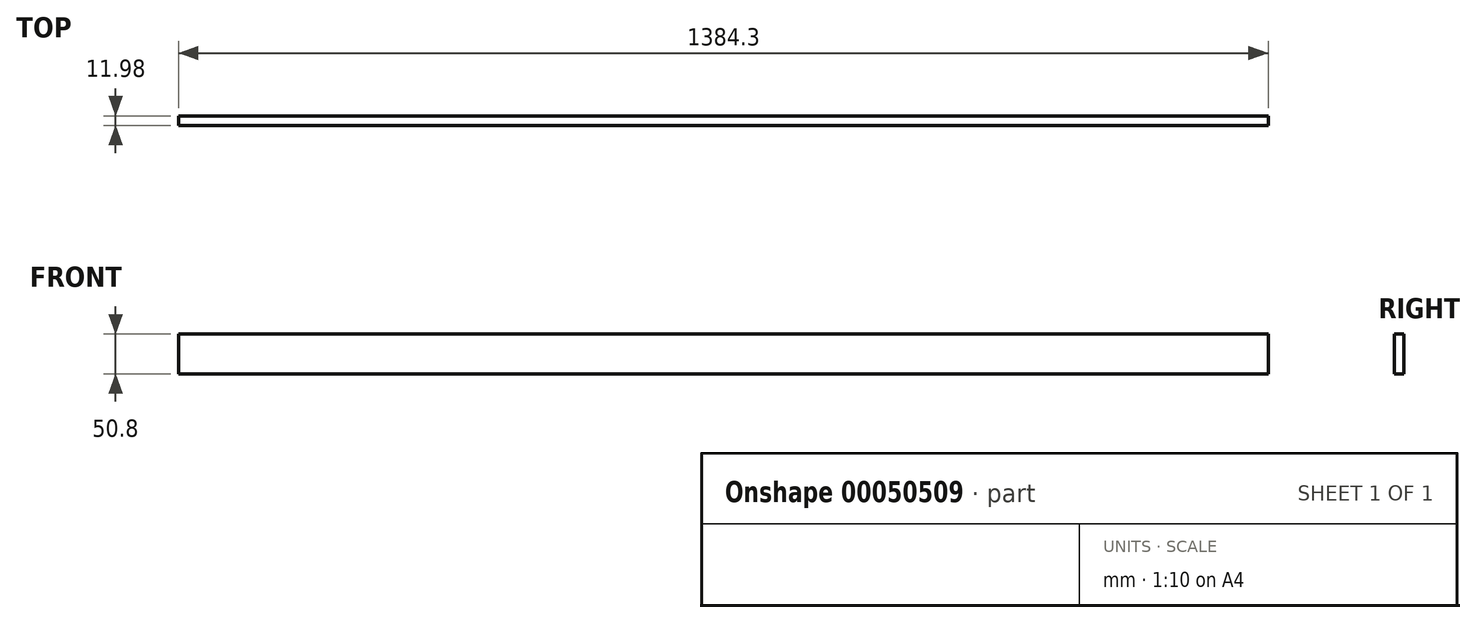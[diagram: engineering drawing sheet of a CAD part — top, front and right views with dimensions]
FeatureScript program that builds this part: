
annotation { "Feature Type Name" : "Feature", "Feature Type Description" : "" }
export const myFeature = defineFeature(function(context is Context, id is Id, definition is map)
    precondition{}
    {
        {
            var Q0;
            Q0=qCreatedBy(makeId("Front.planeOp"),FACE);
            var sketch = newSketch(context, id + "F0", { "sketchPlane" : qUnion([Q0])});
            skLineSegment(sketch, "E0.rect.bottom", {"start": v(692.15, 25.4) * mm, "end": v(-692.15, 25.4) * mm});
            skLineSegment(sketch, "E0.rect.top", {"start": v(692.15, -25.4) * mm, "end": v(-692.15, -25.4) * mm});
            skLineSegment(sketch, "E0.rect.left", {"start": v(692.15, 25.4) * mm, "end": v(692.15, -25.4) * mm});
            skLineSegment(sketch, "E0.rect.right", {"start": v(-692.15, 25.4) * mm, "end": v(-692.15, -25.4) * mm});
            skPoint(sketch, "E0.rect.middle", {"position": v(0, 0) * mm});
            skSolve(sketch);
        }
        {
            var Q0;
            Q0 = qSketchRegion(id + "F0", true);
            extrude(context, id + "F1", {"entities" : qUnion([Q0]), "endBound" : BoundingType.SYMMETRIC, "depth" : 12 * mm});
        }
    });
